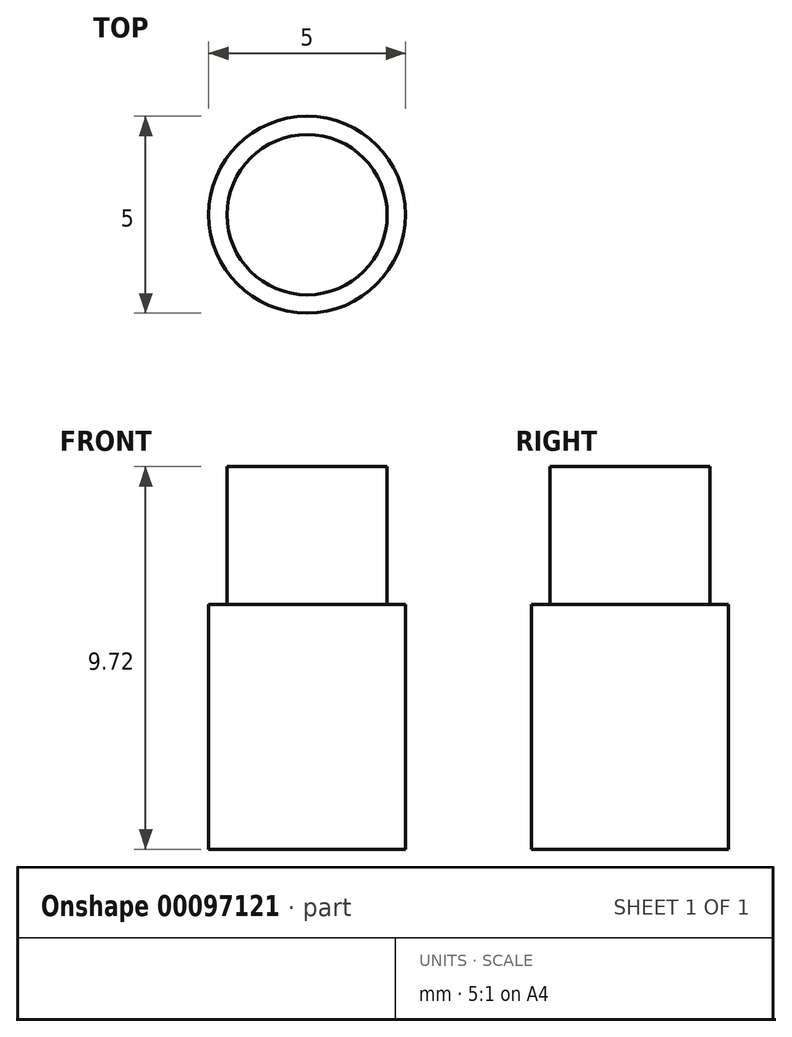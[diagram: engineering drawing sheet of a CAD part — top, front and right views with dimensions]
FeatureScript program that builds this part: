
annotation { "Feature Type Name" : "Feature", "Feature Type Description" : "" }
export const myFeature = defineFeature(function(context is Context, id is Id, definition is map)
    precondition{}
    {
        {
            var Q0;
            Q0=qCreatedBy(makeId("Front.planeOp"),FACE);
            var sketch = newSketch(context, id + "F0", { "sketchPlane" : qUnion([Q0])});
            skLineSegment(sketch, "E0", {"start": v(0, 0) * mm, "end": v(-2.5, 0) * mm});
            skLineSegment(sketch, "E1", {"start": v(-2.5, 0) * mm, "end": v(-2.5, 6.22) * mm});
            skLineSegment(sketch, "E2", {"start": v(-2.5, 6.22) * mm, "end": v(-2.03, 6.22) * mm});
            skLineSegment(sketch, "E3", {"start": v(-2.03, 6.22) * mm, "end": v(-2.03, 9.72) * mm});
            skLineSegment(sketch, "E4", {"start": v(-2.03, 9.72) * mm, "end": v(0, 9.72) * mm});
            skLineSegment(sketch, "E5", {"start": v(0, 9.72) * mm, "end": v(0, 0) * mm});
            skSolve(sketch);
        }
        {
            var Q0;
            Q0=qSketchRegion(id+"F0",true);
            var Q1;
            Q1=sQuery(id+"F0.wireOp",EDGE,"E5");
            revolve(context, id + "F1", {"entities" : qUnion([Q0]), "axis" : qUnion([Q1]), "revolveType" : RevolveType.FULL});
        }
    });
